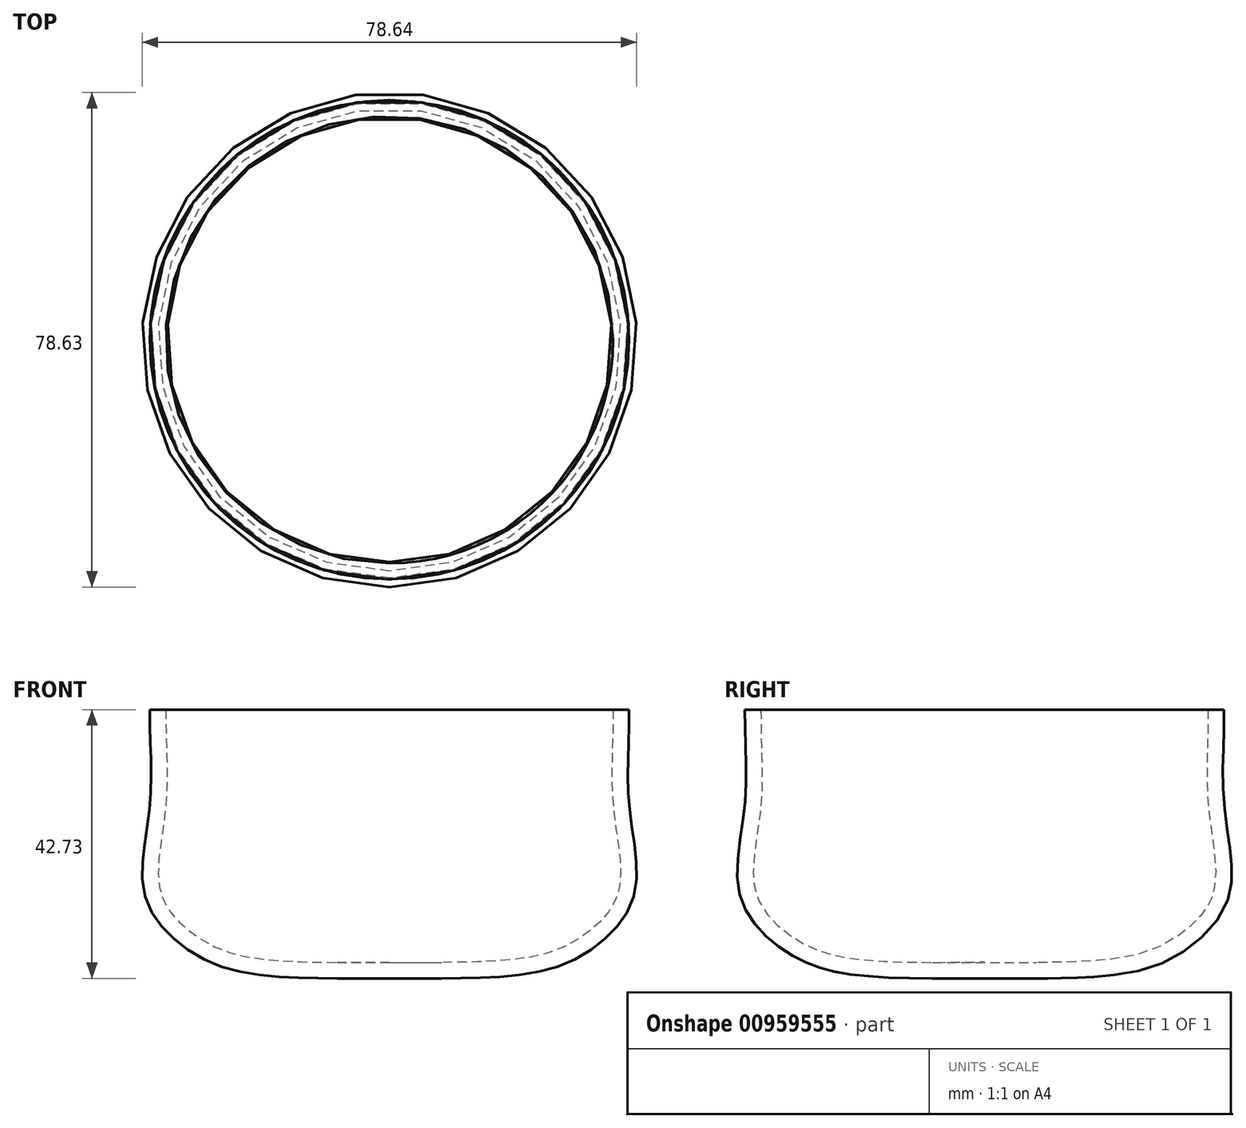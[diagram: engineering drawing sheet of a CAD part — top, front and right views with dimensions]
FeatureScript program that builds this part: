
annotation { "Feature Type Name" : "Feature", "Feature Type Description" : "" }
export const myFeature = defineFeature(function(context is Context, id is Id, definition is map)
    precondition{}
    {
        {
            var Q0;
            Q0=qCreatedBy(makeId("Right.planeOp"),FACE);
            var sketch = newSketch(context, id + "F0", { "sketchPlane" : qUnion([Q0])});
            skLineSegment(sketch, "E0", {"start": v(-31.22, 29.9) * mm, "end": v(-31.22, -12.74) * mm});
            skLineSegment(sketch, "E1", {"start": v(-31.22, 29.9) * mm, "end": v(-69.32, 29.9) * mm});
            skFitSpline(sketch, "E2", {"points": [v(-69.32, 29.9) * mm, v(-69.32, 14.88) * mm, v(-70.02, 0) * mm, v(-62.18, -8.98) * mm, v(-52.46, -12.2) * mm, v(-31.22, -12.74) * mm, v(13.07, -11.84) * mm], "startDerivative": vector(-1.71, -98.28) * mm, "endDerivative": vector(206.71, 1.95) * mm});
            skSolve(sketch);
        }
        {
            var Q0;
            Q0=makeQuery(id+"F0.imprint","IMPRINT",FACE,{"disambiguationData":[TD([[makeQuery(id+"F0.imprint","IMPRINT",EDGE,{"derivedFrom":sQuery(id+"F0.wireOp",EDGE,"E0")}),-1.0]])]});
            var Q1;
            Q1=sQuery(id+"F0.wireOp",EDGE,"E0");
            revolve(context, id + "F1", {"surfaceOperationType" : NewSurfaceOperationType.NEW, "entities" : qUnion([Q0]), "axis" : qUnion([Q1]), "revolveType" : RevolveType.FULL});
        }
        {
            var Q0;
            Q0=makeQuery(id+"F1.opRevolve","SWEPT_FACE",FACE,{"disambiguationData":[OSD([sQuery(id+"F0.wireOp",EDGE,"E1")])]});
            shell(context, id + "F2", {"entities" : qUnion([Q0]), "thickness" : 2.54 * mm});
        }
    });
